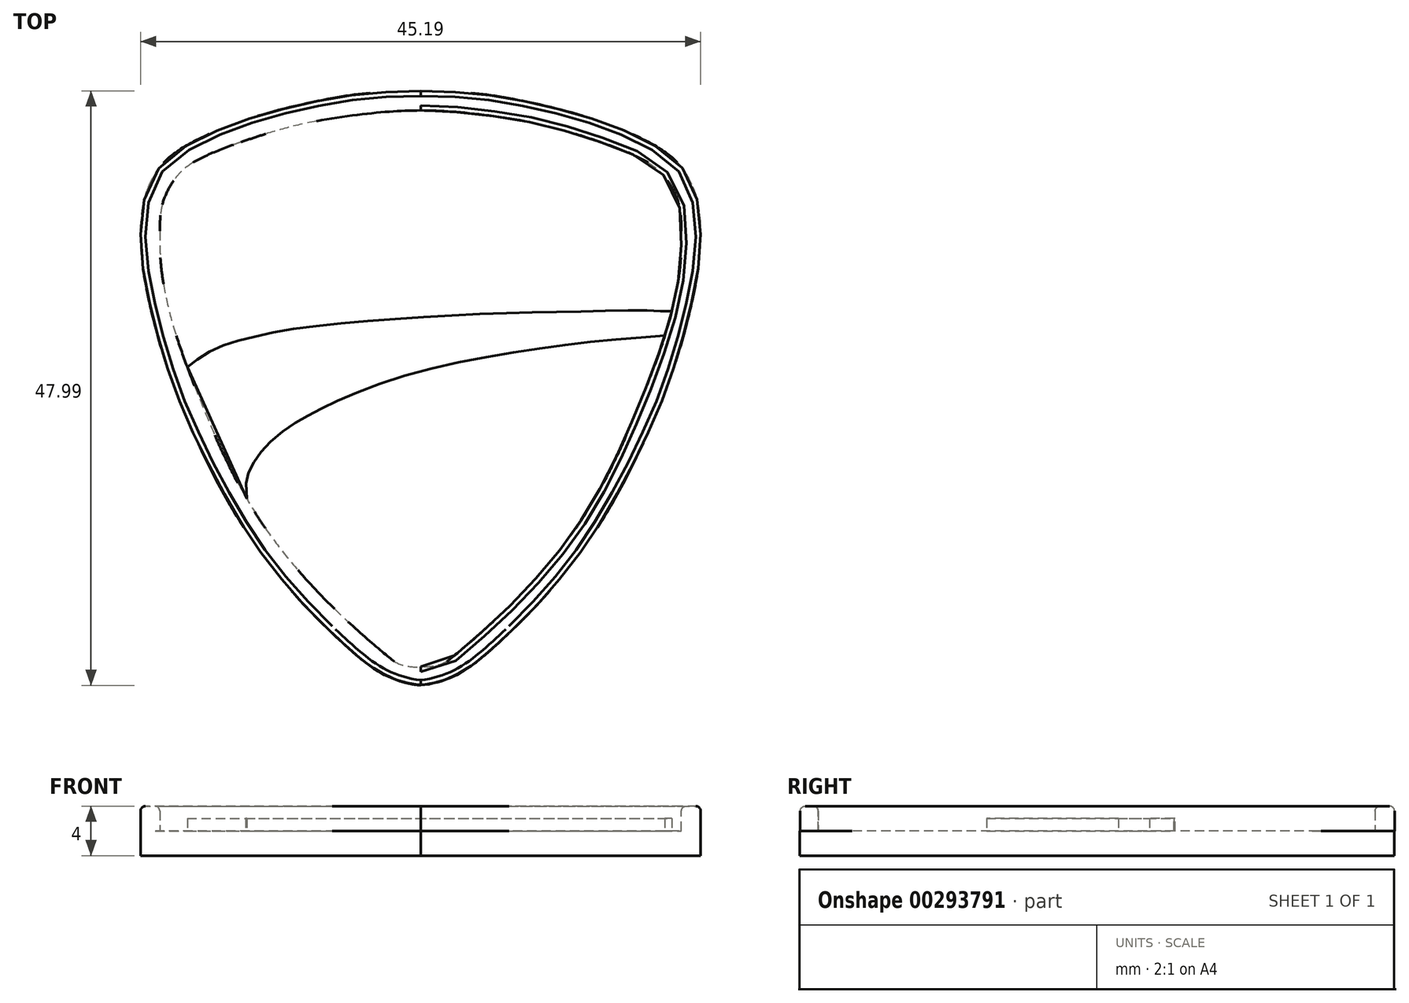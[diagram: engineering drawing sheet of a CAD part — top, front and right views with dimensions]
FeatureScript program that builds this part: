
annotation { "Feature Type Name" : "Feature", "Feature Type Description" : "" }
export const myFeature = defineFeature(function(context is Context, id is Id, definition is map)
    precondition{}
    {
        {
            var Q0;
            Q0=qCreatedBy(makeId("Top.planeOp"),FACE);
            var sketch = newSketch(context, id + "F0", { "sketchPlane" : qUnion([Q0])});
            skFitSpline(sketch, "E0", {"points": [v(-38.68, 29.2) * mm, v(-32.17, 28.73) * mm, v(-24.38, 26.82) * mm, v(-19.43, 24.57) * mm, v(-17.58, 22.99) * mm, v(-16.52, 20.94) * mm, v(-16.12, 18.5) * mm, v(-16.31, 14.78) * mm, v(-18.32, 6.7) * mm, v(-20.75, 0.77) * mm, v(-23.7, -4.83) * mm, v(-27.95, -10.76) * mm, v(-31.68, -14.65) * mm, v(-34.4, -17.03) * mm, v(-36.3, -18.15) * mm, v(-38.68, -18.75) * mm], "startDerivative": vector(119.75, -2.5) * mm, "endDerivative": vector(-50.32, -4.04) * mm});
            skLineSegment(sketch, "E1", {"start": v(-38.68, 29.2) * mm, "end": v(-38.68, -18.81) * mm});
            skFitSpline(sketch, "E2.MirrorCS", {"points": [v(-38.68, 29.2) * mm, v(-45.2, 28.73) * mm, v(-53, 26.82) * mm, v(-57.94, 24.57) * mm, v(-59.8, 22.99) * mm, v(-60.85, 20.94) * mm, v(-61.25, 18.5) * mm, v(-61.06, 14.78) * mm, v(-59.05, 6.7) * mm, v(-56.62, 0.77) * mm, v(-53.68, -4.83) * mm, v(-49.42, -10.76) * mm, v(-45.69, -14.65) * mm, v(-42.98, -17.03) * mm, v(-41.06, -18.15) * mm, v(-38.68, -18.75) * mm], "startDerivative": vector(-119.75, -2.5) * mm, "endDerivative": vector(50.32, -4.04) * mm});
            skPoint(sketch, "E3", {"position": v(-38.68, 5.2) * mm});
            skSolve(sketch);
        }
        {
            var Q0;
            Q0 = qSketchRegion(id + "F0", true);
            extrude(context, id + "F1", {"entities" : qUnion([Q0]), "depth" : 2 * mm, "offsetDistance" : 25 * mm});
        }
        {
            var Q0;
            Q0=makeQuery(id+"F1.opExtrude","CAP_FACE",FACE,{"disambiguationData":[OSD([sQuery(id+"F0.wireOp",EDGE,"E0"),sQuery(id+"F0.wireOp",EDGE,"E2.MirrorCS")])],"isStart":false});
            var sketch = newSketch(context, id + "F2", { "sketchPlane" : qUnion([Q0])});
            skLineSegment(sketch, "E4", {"start": v(-38.68, 29.2) * mm, "end": v(-38.68, -18.75) * mm});
            skFitSpline(sketch, "E5", {"points": [v(-38.68, 27.67) * mm, v(-35.02, 27.47) * mm, v(-29.34, 26.61) * mm, v(-24.52, 25.23) * mm, v(-20.3, 23.44) * mm, v(-18.7, 21.92) * mm, v(-17.85, 20.07) * mm, v(-17.65, 18.22) * mm, v(-17.71, 15.45) * mm, v(-18.38, 11.55) * mm, v(-19.9, 6.86) * mm, v(-23.07, -0.67) * mm, v(-26.83, -7) * mm, v(-31.26, -12.1) * mm, v(-34.23, -14.87) * mm, v(-36.01, -16.39) * mm, v(-36.87, -16.98) * mm, v(-37.93, -17.25) * mm, v(-38.68, -17.25) * mm], "startDerivative": vector(62.08, -0.36) * mm, "endDerivative": vector(-27.6, 1.53) * mm});
            skFitSpline(sketch, "E6.MirrorCS", {"points": [v(-38.68, 27.67) * mm, v(-42.35, 27.47) * mm, v(-48.03, 26.61) * mm, v(-52.85, 25.23) * mm, v(-57.08, 23.44) * mm, v(-58.66, 21.92) * mm, v(-59.52, 20.07) * mm, v(-59.72, 18.22) * mm, v(-59.66, 15.45) * mm, v(-59, 11.55) * mm, v(-57.48, 6.86) * mm, v(-54.3, -0.67) * mm, v(-50.54, -7) * mm, v(-46.11, -12.1) * mm, v(-43.14, -14.87) * mm, v(-41.36, -16.39) * mm, v(-40.5, -16.98) * mm, v(-39.44, -17.25) * mm, v(-38.68, -17.25) * mm], "startDerivative": vector(-62.08, -0.36) * mm, "endDerivative": vector(27.6, 1.53) * mm});
            skPoint(sketch, "E7", {"position": v(-38.68, 5.23) * mm});
            skFitSpline(sketch, "E8", {"points": [v(-38.68, 29.24) * mm, v(-32.17, 28.77) * mm, v(-24.38, 26.85) * mm, v(-19.43, 24.6) * mm, v(-17.58, 23.02) * mm, v(-16.52, 20.97) * mm, v(-16.12, 18.53) * mm, v(-16.28, 15.02) * mm, v(-18.24, 6.94) * mm, v(-20.58, 1.12) * mm, v(-24.32, -5.84) * mm, v(-28.09, -10.92) * mm, v(-31.55, -14.52) * mm, v(-34.4, -17) * mm, v(-36.3, -18.12) * mm, v(-38.68, -18.71) * mm], "startDerivative": vector(119.75, -2.5) * mm, "endDerivative": vector(-50.32, -4.04) * mm});
            skLineSegment(sketch, "E9", {"start": v(-38.68, 29.24) * mm, "end": v(-38.68, -18.78) * mm});
            skFitSpline(sketch, "E10.MirrorCS", {"points": [v(-38.68, 29.24) * mm, v(-45.2, 28.77) * mm, v(-53, 26.85) * mm, v(-57.94, 24.6) * mm, v(-59.8, 23.02) * mm, v(-60.85, 20.97) * mm, v(-61.25, 18.53) * mm, v(-61.1, 15.02) * mm, v(-59.13, 6.94) * mm, v(-56.79, 1.12) * mm, v(-53.05, -5.84) * mm, v(-49.28, -10.92) * mm, v(-45.82, -14.52) * mm, v(-42.98, -17) * mm, v(-41.06, -18.12) * mm, v(-38.68, -18.71) * mm], "startDerivative": vector(-119.75, -2.5) * mm, "endDerivative": vector(50.32, -4.04) * mm});
            skSolve(sketch);
        }
        {
            var Q0;
            Q0 = qSketchRegion(id + "F2", true);
            extrude(context, id + "F3", {"entities" : qUnion([Q0]), "operationType" : NewBodyOperationType.ADD, "depth" : 2 * mm, "offsetDistance" : 25 * mm});
        }
        {
            var Q0;
            Q0=makeQuery(id+"F3.boolean.opBoolean","SPLIT",FACE,{"disambiguationData":[TD([makeQuery(id+"F3.opExtrude","SWEPT_FACE",FACE,{"disambiguationData":[OSD([sQuery(id+"F2.wireOp",EDGE,"E5")])]})])],"derivedFrom":makeQuery(id+"F1.opExtrude","CAP_FACE",FACE,{"disambiguationData":[OSD([sQuery(id+"F0.wireOp",EDGE,"E0"),sQuery(id+"F0.wireOp",EDGE,"E2.MirrorCS")])],"isStart":false})});
            var sketch = newSketch(context, id + "F4", { "sketchPlane" : qUnion([Q0])});
            skFitSpline(sketch, "E11", {"points": [v(-57.5, 6.95) * mm, v(-55.78, 8.18) * mm, v(-53.18, 9.13) * mm, v(-49.11, 10) * mm, v(-41.8, 10.75) * mm, v(-32.62, 11.28) * mm, v(-25.38, 11.44) * mm, v(-20.07, 11.5) * mm, v(-18.4, 11.45) * mm], "startDerivative": vector(15.65, 12) * mm, "endDerivative": vector(22.97, 1.9) * mm});
            skFitSpline(sketch, "E12", {"points": [v(-52.72, -3.68) * mm, v(-52.68, -1.89) * mm, v(-52.1, -0.67) * mm, v(-51.14, 0.57) * mm, v(-49.25, 2.15) * mm, v(-47.51, 3.16) * mm, v(-44.79, 4.49) * mm, v(-39.06, 6.5) * mm, v(-31.6, 8.05) * mm, v(-25.03, 8.98) * mm, v(-18.97, 9.48) * mm], "startDerivative": vector(-4.28, 37.53) * mm, "endDerivative": vector(42.67, 3.35) * mm});
            skLineSegment(sketch, "E13", {"start": v(-57.5, 6.95) * mm, "end": v(-52.72, -3.68) * mm});
            skLineSegment(sketch, "E14", {"start": v(-18.4, 11.45) * mm, "end": v(-18.97, 9.48) * mm});
            skSolve(sketch);
        }
        {
            var Q0;
            Q0 = qSketchRegion(id + "F4", true);
            extrude(context, id + "F5", {"entities" : qUnion([Q0]), "depth" : 1 * mm, "offsetDistance" : 25 * mm});
        }
        {
            var Q0;
            Q0=makeQuery(id+"F3.opExtrude","CAP_FACE",FACE,{"disambiguationData":[OSD([sQuery(id+"F2.wireOp",EDGE,"E5"),sQuery(id+"F2.wireOp",EDGE,"E6.MirrorCS"),sQuery(id+"F2.wireOp",EDGE,"E8"),sQuery(id+"F2.wireOp",EDGE,"E10.MirrorCS")])],"isStart":false});
            fillet(context, id + "F6", {"entities" : qUnion([Q0]), "tangentPropagation" : true, "radius" : .4 * mm, "defaultsChanged" : false, "vertexSettings" : [], "allowEdgeOverflow" : false});
        }
    });
